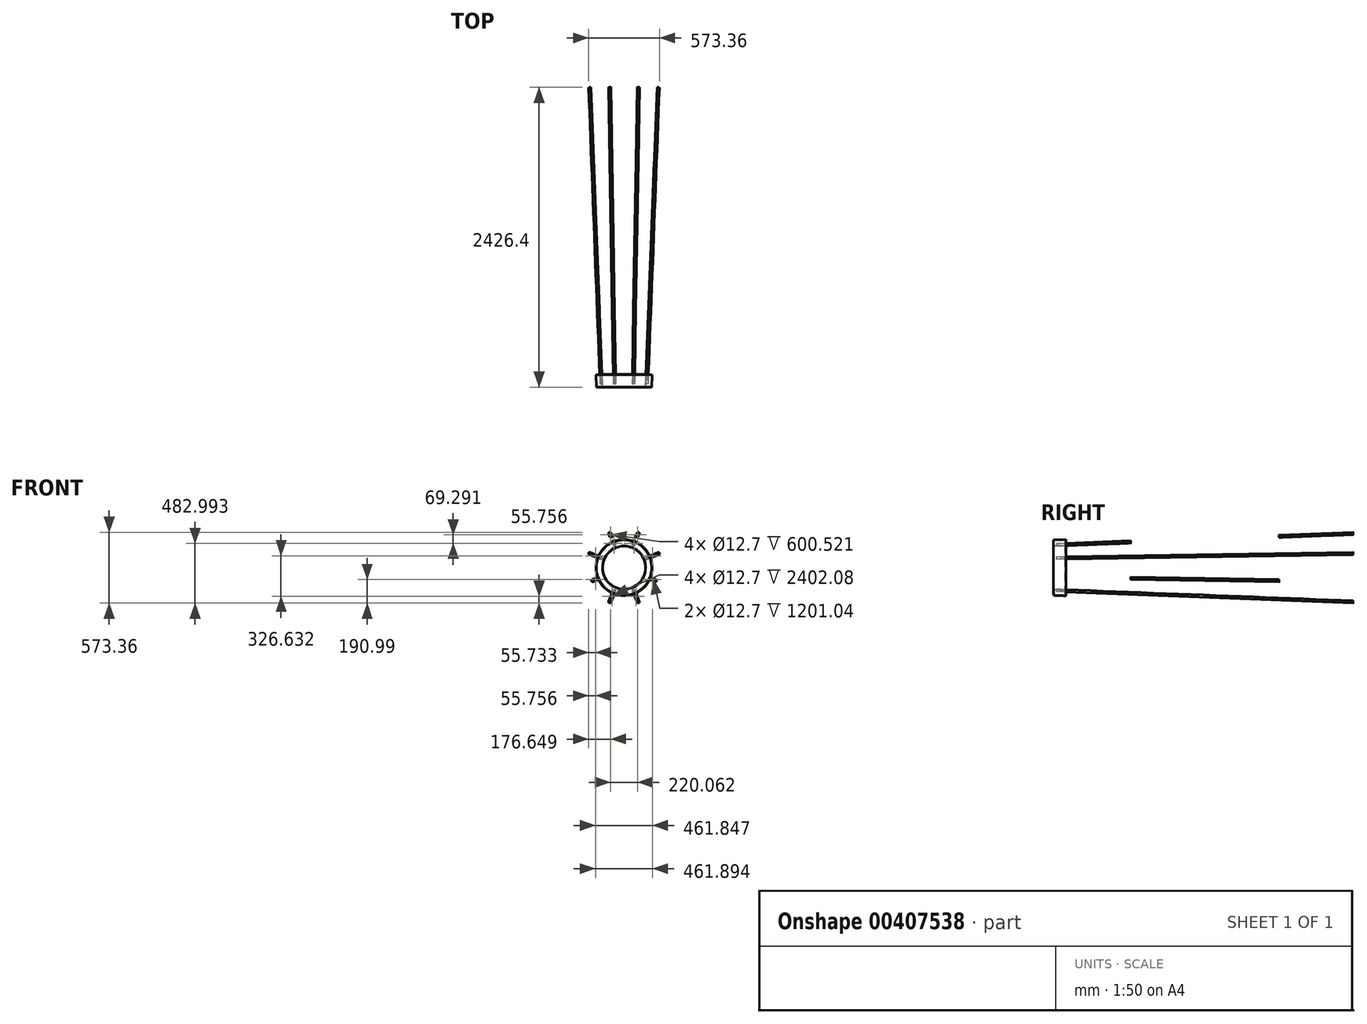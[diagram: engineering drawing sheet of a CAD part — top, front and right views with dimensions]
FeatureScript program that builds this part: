
annotation { "Feature Type Name" : "Feature", "Feature Type Description" : "" }
export const myFeature = defineFeature(function(context is Context, id is Id, definition is map)
    precondition{}
    {
        {
            var Q0;
            Q0=qCreatedBy(makeId("Front.planeOp"),FACE);
            cPlane(context, id + "F0", {"entities" : qUnion([Q0]), "cplaneType" : CPlaneType.OFFSET, "offset" : 1200 * mm, "width" : 150 * mm, "height" : 150 * mm});
        }
        {
            var Q0;
            Q0=qCreatedBy(id+"F0.planeOp",FACE);
            cPlane(context, id + "F1", {"entities" : qUnion([Q0]), "cplaneType" : CPlaneType.OFFSET, "offset" : 600 * mm, "oppositeDirection" : true, "width" : 150 * mm, "height" : 150 * mm});
        }
        {
            var Q0;
            Q0=qCreatedBy(id+"F0.planeOp",FACE);
            cPlane(context, id + "F2", {"entities" : qUnion([Q0]), "cplaneType" : CPlaneType.OFFSET, "offset" : 1800 * mm, "oppositeDirection" : true, "width" : 150 * mm, "height" : 150 * mm});
        }
        {
            var Q0;
            Q0=qCreatedBy(id+"F0.planeOp",FACE);
            cPlane(context, id + "F3", {"entities" : qUnion([Q0]), "cplaneType" : CPlaneType.OFFSET, "offset" : 2400 * mm, "oppositeDirection" : true, "width" : 150 * mm, "height" : 150 * mm});
        }
        {
            var Q0;
            Q0=qCreatedBy(id+"F0.planeOp",FACE);
            var sketch = newSketch(context, id + "F4", { "sketchPlane" : qUnion([Q0])});
            skCircle(sketch, "E0.cCircle", {"center": v(0, 0) * mm, "radius": 200 * mm, "construction": true});
            skLineSegment(sketch, "E0.0", {"start": v(76.54, -184.78) * mm, "end": v(-76.54, -184.78) * mm, "construction": true});
            skLineSegment(sketch, "E0.1", {"start": v(-76.54, -184.78) * mm, "end": v(-184.78, -76.54) * mm, "construction": true});
            skLineSegment(sketch, "E0.2", {"start": v(-184.78, -76.54) * mm, "end": v(-184.78, 76.54) * mm, "construction": true});
            skLineSegment(sketch, "E0.3", {"start": v(-184.78, 76.54) * mm, "end": v(-76.54, 184.78) * mm, "construction": true});
            skLineSegment(sketch, "E0.4", {"start": v(-76.54, 184.78) * mm, "end": v(76.54, 184.78) * mm, "construction": true});
            skLineSegment(sketch, "E0.5", {"start": v(76.54, 184.78) * mm, "end": v(184.78, 76.54) * mm, "construction": true});
            skLineSegment(sketch, "E0.6", {"start": v(184.78, 76.54) * mm, "end": v(184.78, -76.54) * mm, "construction": true});
            skLineSegment(sketch, "E0.7", {"start": v(184.78, -76.54) * mm, "end": v(76.54, -184.78) * mm, "construction": true});
            skSolve(sketch);
        }
        {
            var Q0;
            Q0=qCreatedBy(id+"F3.planeOp",FACE);
            var sketch = newSketch(context, id + "F5", { "sketchPlane" : qUnion([Q0])});
            skCircle(sketch, "E1.cCircle", {"center": v(0, 0) * mm, "radius": 300 * mm, "construction": true});
            skLineSegment(sketch, "E1.0", {"start": v(-277.16, 114.8) * mm, "end": v(-114.8, 277.16) * mm, "construction": true});
            skLineSegment(sketch, "E1.1", {"start": v(-114.8, 277.16) * mm, "end": v(114.8, 277.16) * mm, "construction": true});
            skLineSegment(sketch, "E1.2", {"start": v(114.8, 277.16) * mm, "end": v(277.16, 114.8) * mm, "construction": true});
            skLineSegment(sketch, "E1.3", {"start": v(277.16, 114.8) * mm, "end": v(277.16, -114.8) * mm, "construction": true});
            skLineSegment(sketch, "E1.4", {"start": v(277.16, -114.8) * mm, "end": v(114.8, -277.16) * mm, "construction": true});
            skLineSegment(sketch, "E1.5", {"start": v(114.8, -277.16) * mm, "end": v(-114.8, -277.16) * mm, "construction": true});
            skLineSegment(sketch, "E1.6", {"start": v(-114.8, -277.16) * mm, "end": v(-277.16, -114.8) * mm, "construction": true});
            skLineSegment(sketch, "E1.7", {"start": v(-277.16, -114.8) * mm, "end": v(-277.16, 114.8) * mm, "construction": true});
            skSolve(sketch);
        }
        {
            var Q0;
            Q0=sQuery(id+"F5.wireOp",VERTEX,"E1.4.end");
            var Q1;
            Q1=sQuery(id+"F4.wireOp",VERTEX,"E0.0.start");
            var Q2;
            Q2=sQuery(id+"F4.wireOp",VERTEX,"E0.0.end");
            cPlane(context, id + "F6", {"entities" : qUnion([Q0, Q1, Q2]), "cplaneType" : CPlaneType.THREE_POINT, "offset" : 25 * mm, "width" : 150 * mm, "height" : 150 * mm});
        }
        {
            var Q0;
            Q0=sQuery(id+"F4.wireOp",VERTEX,"E0.1.end");
            var Q1;
            Q1=sQuery(id+"F4.wireOp",VERTEX,"E0.2.end");
            var Q2;
            Q2=sQuery(id+"F5.wireOp",VERTEX,"E1.0.start");
            cPlane(context, id + "F7", {"entities" : qUnion([Q0, Q1, Q2]), "cplaneType" : CPlaneType.THREE_POINT, "offset" : 25 * mm, "width" : 150 * mm, "height" : 150 * mm});
        }
        {
            var Q0;
            Q0=sQuery(id+"F4.wireOp",VERTEX,"E0.6.end");
            var Q1;
            Q1=sQuery(id+"F4.wireOp",VERTEX,"E0.5.end");
            var Q2;
            Q2=sQuery(id+"F5.wireOp",VERTEX,"E1.2.end");
            cPlane(context, id + "F8", {"entities" : qUnion([Q0, Q1, Q2]), "cplaneType" : CPlaneType.THREE_POINT, "offset" : 25 * mm, "width" : 150 * mm, "height" : 150 * mm});
        }
        {
            var Q0;
            Q0=sQuery(id+"F4.wireOp",VERTEX,"E0.4.end");
            var Q1;
            Q1=sQuery(id+"F4.wireOp",VERTEX,"E0.3.end");
            var Q2;
            Q2=sQuery(id+"F5.wireOp",VERTEX,"E1.0.end");
            cPlane(context, id + "F9", {"entities" : qUnion([Q0, Q1, Q2]), "cplaneType" : CPlaneType.THREE_POINT, "offset" : 25 * mm, "width" : 150 * mm, "height" : 150 * mm});
        }
        {
            var Q0;
            Q0=qCreatedBy(id+"F6.planeOp",FACE);
            var sketch = newSketch(context, id + "F10", { "sketchPlane" : qUnion([Q0])});
            skLineSegment(sketch, "E2", {"start": v(76.54, -1192) * mm, "end": v(114.8, 1209.77) * mm, "construction": true});
            skLineSegment(sketch, "E3", {"start": v(-76.54, -1192) * mm, "end": v(-114.8, 1209.77) * mm, "construction": true});
            skSolve(sketch);
        }
        {
            var Q0;
            Q0=qCreatedBy(id+"F7.planeOp",FACE);
            var sketch = newSketch(context, id + "F11", { "sketchPlane" : qUnion([Q0])});
            skLineSegment(sketch, "E4", {"start": v(-1192, 76.54) * mm, "end": v(1209.77, 114.8) * mm, "construction": true});
            skLineSegment(sketch, "E5", {"start": v(-1192, -76.54) * mm, "end": v(1209.77, -114.8) * mm, "construction": true});
            skSolve(sketch);
        }
        {
            var Q0;
            Q0=qCreatedBy(id+"F9.planeOp",FACE);
            var sketch = newSketch(context, id + "F12", { "sketchPlane" : qUnion([Q0])});
            skLineSegment(sketch, "E6", {"start": v(114.8, 1209.77) * mm, "end": v(76.54, -1192) * mm, "construction": true});
            skLineSegment(sketch, "E7", {"start": v(-114.8, 1209.77) * mm, "end": v(-76.54, -1192) * mm, "construction": true});
            skSolve(sketch);
        }
        {
            var Q0;
            Q0=qCreatedBy(id+"F1.planeOp",FACE);
            var sketch = newSketch(context, id + "F13", { "sketchPlane" : qUnion([Q0])});
            skCircle(sketch, "E8.cCircle", {"center": v(0, 0) * mm, "radius": 207.87 * mm, "construction": true});
            skLineSegment(sketch, "E8.0", {"start": v(207.87, -86.1) * mm, "end": v(86.1, -207.87) * mm, "construction": true});
            skLineSegment(sketch, "E8.1", {"start": v(86.1, -207.87) * mm, "end": v(-86.1, -207.87) * mm, "construction": true});
            skLineSegment(sketch, "E8.2", {"start": v(-86.1, -207.87) * mm, "end": v(-207.87, -86.1) * mm, "construction": true});
            skLineSegment(sketch, "E8.3", {"start": v(-207.87, -86.1) * mm, "end": v(-207.87, 86.1) * mm, "construction": true});
            skLineSegment(sketch, "E8.4", {"start": v(-207.87, 86.1) * mm, "end": v(-86.1, 207.87) * mm, "construction": true});
            skLineSegment(sketch, "E8.5", {"start": v(-86.1, 207.87) * mm, "end": v(86.1, 207.87) * mm, "construction": true});
            skLineSegment(sketch, "E8.6", {"start": v(86.1, 207.87) * mm, "end": v(207.87, 86.1) * mm, "construction": true});
            skLineSegment(sketch, "E8.7", {"start": v(207.87, 86.1) * mm, "end": v(207.87, -86.1) * mm, "construction": true});
            skPoint(sketch, "E8.0.midPoint", {"position": v(146.99, -146.99) * mm});
            skSolve(sketch);
        }
        {
            var Q0;
            Q0=qCreatedBy(id+"F2.planeOp",FACE);
            var sketch = newSketch(context, id + "F14", { "sketchPlane" : qUnion([Q0])});
            skCircle(sketch, "E9.cCircle", {"center": v(0, 0) * mm, "radius": 254.07 * mm, "construction": true});
            skLineSegment(sketch, "E9.0", {"start": v(254.07, -105.24) * mm, "end": v(105.24, -254.07) * mm, "construction": true});
            skLineSegment(sketch, "E9.1", {"start": v(105.24, -254.07) * mm, "end": v(-105.24, -254.07) * mm, "construction": true});
            skLineSegment(sketch, "E9.2", {"start": v(-105.24, -254.07) * mm, "end": v(-254.07, -105.24) * mm, "construction": true});
            skLineSegment(sketch, "E9.3", {"start": v(-254.07, -105.24) * mm, "end": v(-254.07, 105.24) * mm, "construction": true});
            skLineSegment(sketch, "E9.4", {"start": v(-254.07, 105.24) * mm, "end": v(-105.24, 254.07) * mm, "construction": true});
            skLineSegment(sketch, "E9.5", {"start": v(-105.24, 254.07) * mm, "end": v(105.24, 254.07) * mm, "construction": true});
            skLineSegment(sketch, "E9.6", {"start": v(105.24, 254.07) * mm, "end": v(254.07, 105.24) * mm, "construction": true});
            skLineSegment(sketch, "E9.7", {"start": v(254.07, 105.24) * mm, "end": v(254.07, -105.24) * mm, "construction": true});
            skPoint(sketch, "E9.0.midPoint", {"position": v(179.65, -179.65) * mm});
            skSolve(sketch);
        }
        {
            var Q0;
            Q0=sQuery(id+"F4.wireOp",VERTEX,"E0.0.end");
            var Q1;
            Q1=sQuery(id+"F10.wireOp",EDGE,"E3");
            cPlane(context, id + "F15", {"entities" : qUnion([Q0, Q1]), "cplaneType" : CPlaneType.LINE_POINT, "offset" : 25 * mm, "width" : 150 * mm, "height" : 150 * mm});
        }
        {
            var Q0;
            Q0=qCreatedBy(id+"F15.planeOp",FACE);
            var sketch = newSketch(context, id + "F16", { "sketchPlane" : qUnion([Q0])});
            skCircle(sketch, "E10", {"center": v(95.52, -230.8) * mm, "radius": 6.35 * mm});
            skCircle(sketch, "E11", {"center": v(95.52, -230.8) * mm, "radius": 9.53 * mm});
            skSolve(sketch);
        }
        {
            var Q0;
            Q0 = qSketchRegion(id + "F16", true);
            var Q1;
            Q1=sQuery(id+"F5.wireOp",VERTEX,"E1.5.end");
            extrude(context, id + "F17", {"entities" : qUnion([Q0]), "endBound" : BoundingType.UP_TO_VERTEX, "depth" : 25 * mm, "endBoundEntityVertex" : qUnion([Q1]), "offsetDistance" : 25 * mm});
        }
        {
            var Q0;
            Q0=sQuery(id+"F11.wireOp",EDGE,"E5");
            var Q1;
            Q1=sQuery(id+"F13.wireOp",VERTEX,"E8.2.end");
            cPlane(context, id + "F18", {"entities" : qUnion([Q0, Q1]), "cplaneType" : CPlaneType.LINE_POINT, "offset" : 25 * mm, "width" : 150 * mm, "height" : 150 * mm});
        }
        {
            var Q0;
            Q0=qCreatedBy(id+"F18.planeOp",FACE);
            var sketch = newSketch(context, id + "F19", { "sketchPlane" : qUnion([Q0])});
            skCircle(sketch, "E12", {"center": v(230.74, -95.66) * mm, "radius": 9.53 * mm});
            skCircle(sketch, "E13", {"center": v(230.74, -95.66) * mm, "radius": 6.35 * mm});
            skSolve(sketch);
        }
        {
            var Q0;
            Q0 = qSketchRegion(id + "F19", true);
            var Q1;
            Q1=sQuery(id+"F14.wireOp",VERTEX,"E9.2.end");
            extrude(context, id + "F20", {"entities" : qUnion([Q0]), "endBound" : BoundingType.UP_TO_VERTEX, "depth" : 25 * mm, "endBoundEntityVertex" : qUnion([Q1]), "offsetDistance" : 1000 * mm, "offsetOppositeDirection" : true});
        }
        {
            var Q0;
            Q0=sQuery(id+"F11.wireOp",EDGE,"E4");
            var Q1;
            Q1=sQuery(id+"F4.wireOp",VERTEX,"E0.2.end");
            cPlane(context, id + "F21", {"entities" : qUnion([Q0, Q1]), "cplaneType" : CPlaneType.LINE_POINT, "offset" : 25 * mm, "width" : 150 * mm, "height" : 150 * mm});
        }
        {
            var Q0;
            Q0=qCreatedBy(id+"F21.planeOp",FACE);
            var sketch = newSketch(context, id + "F22", { "sketchPlane" : qUnion([Q0])});
            skCircle(sketch, "E14", {"center": v(230.74, 95.66) * mm, "radius": 9.53 * mm});
            skCircle(sketch, "E15", {"center": v(230.74, 95.66) * mm, "radius": 6.35 * mm});
            skSolve(sketch);
        }
        {
            var Q0;
            Q0 = qSketchRegion(id + "F22", true);
            var Q1;
            Q1=sQuery(id+"F11.wireOp",VERTEX,"E4.end");
            extrude(context, id + "F23", {"entities" : qUnion([Q0]), "endBound" : BoundingType.UP_TO_VERTEX, "depth" : 25 * mm, "endBoundEntityVertex" : qUnion([Q1]), "offsetDistance" : 25 * mm});
        }
        {
            var Q0;
            Q0=sQuery(id+"F12.wireOp",EDGE,"E7");
            var Q1;
            Q1=sQuery(id+"F4.wireOp",VERTEX,"E0.3.end");
            cPlane(context, id + "F24", {"entities" : qUnion([Q0, Q1]), "cplaneType" : CPlaneType.LINE_POINT, "offset" : 25 * mm, "width" : 150 * mm, "height" : 150 * mm});
        }
        {
            var Q0;
            Q0=qCreatedBy(id+"F24.planeOp",FACE);
            var sketch = newSketch(context, id + "F25", { "sketchPlane" : qUnion([Q0])});
            skCircle(sketch, "E16", {"center": v(-95.52, 230.8) * mm, "radius": 9.53 * mm});
            skCircle(sketch, "E17", {"center": v(-95.52, 230.8) * mm, "radius": 6.35 * mm});
            skSolve(sketch);
        }
        {
            var Q0;
            Q0 = qSketchRegion(id + "F25", true);
            var Q1;
            Q1=sQuery(id+"F13.wireOp",VERTEX,"E8.4.end");
            extrude(context, id + "F26", {"entities" : qUnion([Q0]), "endBound" : BoundingType.UP_TO_VERTEX, "oppositeDirection" : true, "depth" : 25 * mm, "endBoundEntityVertex" : qUnion([Q1]), "offsetDistance" : 25 * mm});
        }
        {
            var Q0;
            Q0=sQuery(id+"F12.wireOp",EDGE,"E7");
            var Q1;
            Q1=sQuery(id+"F14.wireOp",VERTEX,"E9.4.end");
            cPlane(context, id + "F27", {"entities" : qUnion([Q0, Q1]), "cplaneType" : CPlaneType.LINE_POINT, "offset" : 25 * mm, "width" : 150 * mm, "height" : 150 * mm});
        }
        {
            var Q0;
            Q0=qCreatedBy(id+"F27.planeOp",FACE);
            var sketch = newSketch(context, id + "F28", { "sketchPlane" : qUnion([Q0])});
            skCircle(sketch, "E18", {"center": v(-95.52, 230.8) * mm, "radius": 6.35 * mm});
            skCircle(sketch, "E19", {"center": v(-95.52, 230.8) * mm, "radius": 9.53 * mm});
            skSolve(sketch);
        }
        {
            var Q0;
            Q0 = qSketchRegion(id + "F28", true);
            var Q1;
            Q1=sQuery(id+"F5.wireOp",VERTEX,"E1.0.end");
            extrude(context, id + "F29", {"entities" : qUnion([Q0]), "endBound" : BoundingType.UP_TO_VERTEX, "oppositeDirection" : true, "depth" : 25 * mm, "endBoundEntityVertex" : qUnion([Q1]), "offsetDistance" : 25 * mm});
        }
        {
            var Q0;
            Q0=makeQuery(id+"F17.opExtrude","SWEPT_BODY",BODY,{"disambiguationData":[OSD([sQuery(id+"F16.wireOp",EDGE,"E10"),sQuery(id+"F16.wireOp",EDGE,"E11")])]});
            var Q1;
            Q1=makeQuery(id+"F20.opExtrude","SWEPT_BODY",BODY,{"disambiguationData":[OSD([sQuery(id+"F19.wireOp",EDGE,"E12"),sQuery(id+"F19.wireOp",EDGE,"E13")])]});
            var Q2;
            Q2=makeQuery(id+"F23.opExtrude","SWEPT_BODY",BODY,{"disambiguationData":[OSD([sQuery(id+"F22.wireOp",EDGE,"E14"),sQuery(id+"F22.wireOp",EDGE,"E15")])]});
            var Q3;
            Q3=makeQuery(id+"F26.opExtrude","SWEPT_BODY",BODY,{"disambiguationData":[OSD([sQuery(id+"F25.wireOp",EDGE,"E16"),sQuery(id+"F25.wireOp",EDGE,"E17")])]});
            var Q4;
            Q4=makeQuery(id+"F29.opExtrude","SWEPT_BODY",BODY,{"disambiguationData":[OSD([sQuery(id+"F28.wireOp",EDGE,"E18"),sQuery(id+"F28.wireOp",EDGE,"E19")])]});
            var Q5;
            Q5=qCreatedBy(makeId("Right.planeOp"),FACE);
            mirror(context, id + "F30", {"entities" : qUnion([Q0, Q1, Q2, Q3, Q4]), "mirrorPlane" : qUnion([Q5])});
        }
        {
            var Q0;
            Q0=sQuery(id+"F5.wireOp",VERTEX,"E1.cCircle.center");
            var Q1;
            Q1=sQuery(id+"F4.wireOp",VERTEX,"E0.cCircle.center");
            var Q2;
            Q2=sQuery(id+"F4.wireOp",VERTEX,"E0.0.end");
            cPlane(context, id + "F31", {"entities" : qUnion([Q0, Q1, Q2]), "cplaneType" : CPlaneType.THREE_POINT, "offset" : 25 * mm, "width" : 150 * mm, "height" : 150 * mm});
        }
        {
            var Q0;
            Q0=qCreatedBy(id+"F31.planeOp",FACE);
            var sketch = newSketch(context, id + "F32", { "sketchPlane" : qUnion([Q0])});
            skLineSegment(sketch, "E20", {"start": v(1124, -178.14) * mm, "end": v(1126.08, -228.1) * mm});
            skLineSegment(sketch, "E21", {"start": v(1124, -178.14) * mm, "end": v(1223.92, -173.98) * mm});
            skLineSegment(sketch, "E22", {"start": v(1226, -223.94) * mm, "end": v(1126.08, -228.1) * mm});
            skLineSegment(sketch, "E23", {"start": v(1124, -178.14) * mm, "end": v(1226, -223.94) * mm, "construction": true});
            skLineSegment(sketch, "E24", {"start": v(1223.92, -173.98) * mm, "end": v(1226, -223.94) * mm});
            skLineSegment(sketch, "E25", {"start": v(1223.92, -173.98) * mm, "end": v(1126.08, -228.1) * mm, "construction": true});
            skPoint(sketch, "E26", {"position": v(1175, -201.04) * mm});
            skLineSegment(sketch, "E27", {"start": v(1128.17, -181.97) * mm, "end": v(1220.09, -178.14) * mm});
            skLineSegment(sketch, "E28", {"start": v(1128.17, -181.97) * mm, "end": v(1129.91, -223.94) * mm});
            skLineSegment(sketch, "E29", {"start": v(1129.91, -223.94) * mm, "end": v(1221.83, -220.1) * mm});
            skLineSegment(sketch, "E30", {"start": v(1221.83, -220.1) * mm, "end": v(1220.09, -178.14) * mm});
            skLineSegment(sketch, "E31", {"start": v(1200, 0) * mm, "end": v(-1200, 0) * mm, "construction": true});
            skSolve(sketch);
        }
        {
            var Q0;
            Q0 = qSketchRegion(id + "F32", true);
            var Q1;
            Q1 = qConstructionFilter(qBodyType(qCreatedBy(id + "F32" ,EDGE), BodyType.WIRE), ConstructionObject.NO);
            var Q2;
            Q2=sQuery(id+"F32.wireOp",EDGE,"E31");
            revolve(context, id + "F33", {"surfaceOperationType" : NewSurfaceOperationType.NEW, "entities" : qUnion([Q0]), "surfaceEntities" : qUnion([Q1]), "axis" : qUnion([Q2]), "revolveType" : RevolveType.FULL});
        }
        {
            var Q0;
            Q0=makeQuery(id+"F17.opExtrude","SWEPT_BODY",BODY,{"disambiguationData":[OSD([sQuery(id+"F16.wireOp",EDGE,"E10"),sQuery(id+"F16.wireOp",EDGE,"E11")])]});
            var Q1;
            Q1=makeQuery(id+"F20.opExtrude","SWEPT_BODY",BODY,{"disambiguationData":[OSD([sQuery(id+"F19.wireOp",EDGE,"E12"),sQuery(id+"F19.wireOp",EDGE,"E13")])]});
            var Q2;
            Q2=makeQuery(id+"F23.opExtrude","SWEPT_BODY",BODY,{"disambiguationData":[OSD([sQuery(id+"F22.wireOp",EDGE,"E14"),sQuery(id+"F22.wireOp",EDGE,"E15")])]});
            var Q3;
            Q3=makeQuery(id+"F26.opExtrude","SWEPT_BODY",BODY,{"disambiguationData":[OSD([sQuery(id+"F25.wireOp",EDGE,"E16"),sQuery(id+"F25.wireOp",EDGE,"E17")])]});
            var Q4;
            Q4=makeQuery(id+"F30.opPattern","COPY",BODY,{"derivedFrom":makeQuery(id+"F17.opExtrude","SWEPT_BODY",BODY,{"disambiguationData":[OSD([sQuery(id+"F16.wireOp",EDGE,"E10"),sQuery(id+"F16.wireOp",EDGE,"E11")])]}),"instanceName":"1"});
            var Q5;
            Q5=makeQuery(id+"F30.opPattern","COPY",BODY,{"derivedFrom":makeQuery(id+"F20.opExtrude","SWEPT_BODY",BODY,{"disambiguationData":[OSD([sQuery(id+"F19.wireOp",EDGE,"E12"),sQuery(id+"F19.wireOp",EDGE,"E13")])]}),"instanceName":"1"});
            var Q6;
            Q6=makeQuery(id+"F30.opPattern","COPY",BODY,{"derivedFrom":makeQuery(id+"F23.opExtrude","SWEPT_BODY",BODY,{"disambiguationData":[OSD([sQuery(id+"F22.wireOp",EDGE,"E14"),sQuery(id+"F22.wireOp",EDGE,"E15")])]}),"instanceName":"1"});
            var Q7;
            Q7=makeQuery(id+"F30.opPattern","COPY",BODY,{"derivedFrom":makeQuery(id+"F26.opExtrude","SWEPT_BODY",BODY,{"disambiguationData":[OSD([sQuery(id+"F25.wireOp",EDGE,"E16"),sQuery(id+"F25.wireOp",EDGE,"E17")])]}),"instanceName":"1"});
            var Q8;
            Q8=makeQuery(id+"F33.opRevolve","SWEPT_BODY",BODY,{"disambiguationData":[OSD([sQuery(id+"F32.wireOp",EDGE,"E20"),sQuery(id+"F32.wireOp",EDGE,"E21"),sQuery(id+"F32.wireOp",EDGE,"E22"),sQuery(id+"F32.wireOp",EDGE,"E24"),sQuery(id+"F32.wireOp",EDGE,"E27"),sQuery(id+"F32.wireOp",EDGE,"E28"),sQuery(id+"F32.wireOp",EDGE,"E29"),sQuery(id+"F32.wireOp",EDGE,"E30")])]});
            booleanBodies(context, id + "F34", {"operationType" : BooleanOperationType.SUBTRACTION, "tools" : qUnion([Q0, Q1, Q2, Q3, Q4, Q5, Q6, Q7]), "targets" : qUnion([Q8]), "keepTools" : true});
        }
    });
